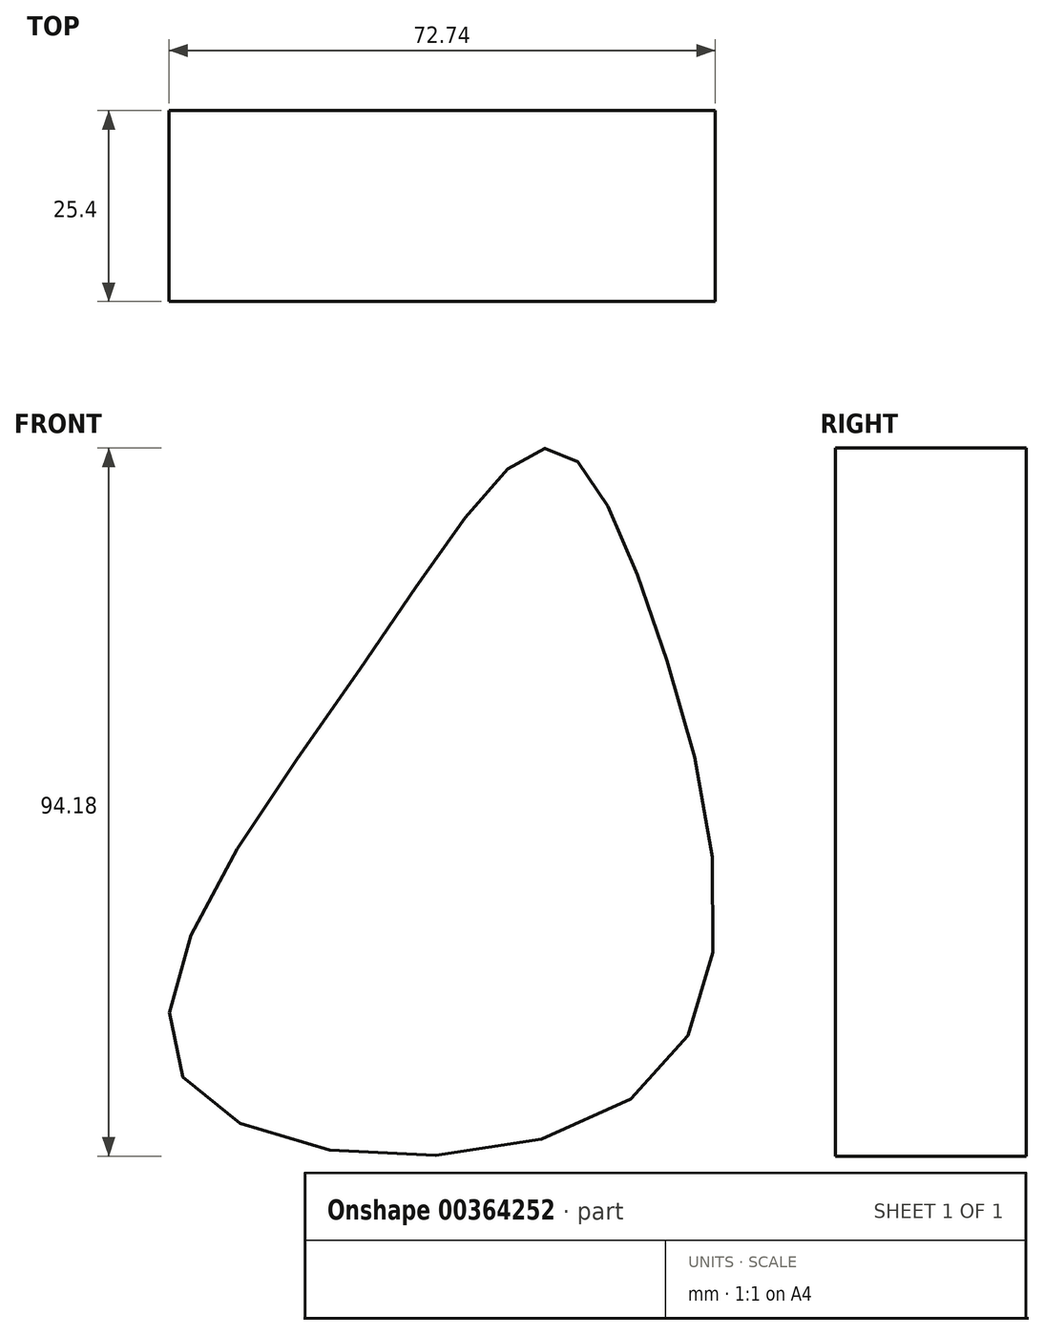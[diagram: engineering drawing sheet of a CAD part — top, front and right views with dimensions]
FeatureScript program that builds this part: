
annotation { "Feature Type Name" : "Feature", "Feature Type Description" : "" }
export const myFeature = defineFeature(function(context is Context, id is Id, definition is map)
    precondition{}
    {
        {
            var Q0;
            Q0=qCreatedBy(makeId("Front.planeOp"),FACE);
            var sketch = newSketch(context, id + "F0", { "sketchPlane" : qUnion([Q0])});
            skFitSpline(sketch, "E0", {"points": [v(-38.83, 54.93) * mm, v(-13.66, 84.39) * mm, v(0, 62.2) * mm, v(0, 0) * mm, v(-61.87, 0) * mm, v(-38.83, 54.93) * mm]});
            skSolve(sketch);
        }
        {
            var Q0;
            Q0=makeQuery(id+"F0.imprint","IMPRINT",FACE,{"disambiguationData":[TD([[makeQuery(id+"F0.imprint","IMPRINT",EDGE,{"derivedFrom":sQuery(id+"F0.wireOp",EDGE,"E0")}),-1.0]])]});
            extrude(context, id + "F1", {"entities" : qUnion([Q0]), "depth" : 25.4 * mm});
        }
    });
